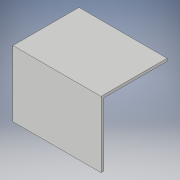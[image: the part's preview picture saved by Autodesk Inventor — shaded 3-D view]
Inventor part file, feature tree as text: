
AUTODESK INVENTOR PART (.ipt)
format: ipt  version: 2017 (Build 210142000, 142)  size: 91,648 bytes
history: native  units: in
note: dims shown in document units (in); Inventor stores cm internally (conversion verified against a paired STEP export)
features: extrude x1, sketch x1
ambient origin geometry x8: Origin, YZ Plane, XZ Plane, XY Plane, X Axis, Y Axis, Z Axis, Center Point
bodies: Solid1 (feature_tree)
feature tree (2):
  extrude  "Extrusion1"  Depth=1.5in
  sketch  "Sketch1"  dims[d0=1.5in d1=1.5in d2=0.0625in d3=1.4375in d4=1.4375in d5=2.0in d6=0.0in]
